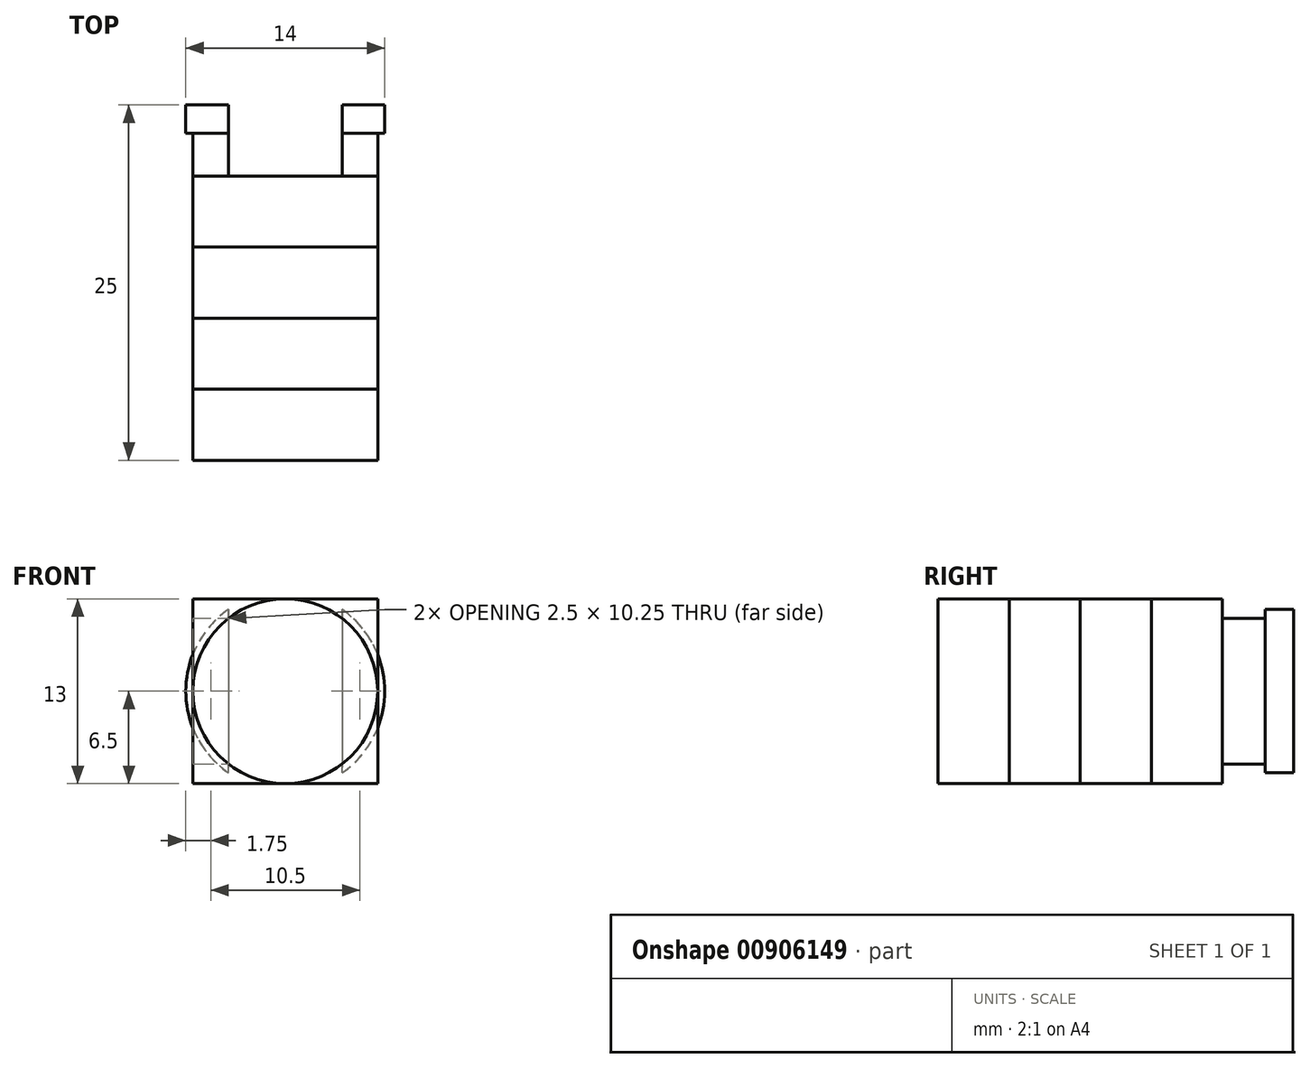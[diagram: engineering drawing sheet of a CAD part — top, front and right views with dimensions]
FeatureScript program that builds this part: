
annotation { "Feature Type Name" : "Feature", "Feature Type Description" : "" }
export const myFeature = defineFeature(function(context is Context, id is Id, definition is map)
    precondition{}
    {
        {
            var Q0;
            Q0=qCreatedBy(makeId("Front.planeOp"),FACE);
            var sketch = newSketch(context, id + "F0", { "sketchPlane" : qUnion([Q0])});
            skCircle(sketch, "E0", {"center": v(0, 0) * mm, "radius": 6.5 * mm});
            skLineSegment(sketch, "E1.rect.bottom", {"start": v(-4, 9.84) * mm, "end": v(4, 9.84) * mm});
            skLineSegment(sketch, "E1.rect.top", {"start": v(-4, -9.84) * mm, "end": v(4, -9.84) * mm});
            skLineSegment(sketch, "E1.rect.left", {"start": v(-4, 9.84) * mm, "end": v(-4, -9.84) * mm});
            skLineSegment(sketch, "E1.rect.right", {"start": v(4, 9.84) * mm, "end": v(4, -9.84) * mm});
            skLineSegment(sketch, "E2", {"start": v(11.65, 0) * mm, "end": v(-11.24, 0) * mm, "construction": true});
            skLineSegment(sketch, "E3", {"start": v(0, -11.93) * mm, "end": v(0, 15.17) * mm, "construction": true});
            skLineSegment(sketch, "E4.rect.bottom", {"start": v(-6.5, -6.5) * mm, "end": v(6.5, -6.5) * mm});
            skLineSegment(sketch, "E4.rect.top", {"start": v(-6.5, 6.5) * mm, "end": v(6.5, 6.5) * mm});
            skLineSegment(sketch, "E4.rect.left", {"start": v(-6.5, -6.5) * mm, "end": v(-6.5, 6.5) * mm});
            skLineSegment(sketch, "E4.rect.right", {"start": v(6.5, -6.5) * mm, "end": v(6.5, 6.5) * mm});
            skSolve(sketch);
        }
        {
            var Q0;
            {var subQ0=sQuery(id+"F0.wireOp",EDGE,"E1.rect.right");var subQ1=sQuery(id+"F0.wireOp",EDGE,"E0");var subQ2=makeQuery(id+"F0.imprint","INTERSECT",VERTEX,{"disambiguationData":[OD(0.0)],"derivedFrom":[subQ1,subQ0]});Q0=makeQuery(id+"F0.imprint","IMPRINT",FACE,{"disambiguationData":[TD([[makeQuery(id+"F0.imprint","IMPRINT",EDGE,{"disambiguationData":[TD([[subQ2,1.0]])],"derivedFrom":subQ1}),1.0]])]});}
            var Q1;
            {var subQ0=sQuery(id+"F0.wireOp",EDGE,"E1.rect.left");var subQ1=sQuery(id+"F0.wireOp",EDGE,"E0");var subQ2=makeQuery(id+"F0.imprint","INTERSECT",VERTEX,{"disambiguationData":[OD(0.0)],"derivedFrom":[subQ1,subQ0]});Q1=makeQuery(id+"F0.imprint","IMPRINT",FACE,{"disambiguationData":[TD([[makeQuery(id+"F0.imprint","IMPRINT",EDGE,{"disambiguationData":[TD([[subQ2,-1.0]])],"derivedFrom":subQ1}),1.0]])]});}
            extrude(context, id + "F1", {"entities" : qUnion([Q0, Q1]), "depth" : 5 * mm});
        }
        {
            var Q0;
            {var subQ0=sQuery(id+"F0.wireOp",EDGE,"E0");var subQ2=sQuery(id+"F0.wireOp",EDGE,"E1.rect.right");var subQ4=makeQuery(id+"F0.imprint","INTERSECT",VERTEX,{"disambiguationData":[OD(0.0)],"derivedFrom":[subQ0,subQ2]});Q0=makeQuery(id+"F0.imprint","IMPRINT",FACE,{"disambiguationData":[TD([[makeQuery(id+"F0.imprint","IMPRINT",EDGE,{"disambiguationData":[TD([[subQ4,-1.0]])],"derivedFrom":subQ0}),1.0]])]});}
            var Q1;
            {var subQ0=sQuery(id+"F0.wireOp",EDGE,"E1.rect.right");var subQ1=sQuery(id+"F0.wireOp",EDGE,"E0");var subQ2=makeQuery(id+"F0.imprint","INTERSECT",VERTEX,{"disambiguationData":[OD(0.0)],"derivedFrom":[subQ1,subQ0]});Q1=makeQuery(id+"F0.imprint","IMPRINT",FACE,{"disambiguationData":[TD([[makeQuery(id+"F0.imprint","IMPRINT",EDGE,{"disambiguationData":[TD([[subQ2,-1.0]])],"derivedFrom":subQ1}),-1.0]])]});}
            var Q2;
            {var subQ1=sQuery(id+"F0.wireOp",EDGE,"E1.rect.bottom");Q2=makeQuery(id+"F0.imprint","IMPRINT",FACE,{"disambiguationData":[TD([[makeQuery(id+"F0.imprint","IMPRINT",EDGE,{"derivedFrom":subQ1}),-1.0]])]});}
            var Q3;
            {var subQ0=sQuery(id+"F0.wireOp",EDGE,"E4.rect.top");var subQ1=sQuery(id+"F0.wireOp",EDGE,"E0");var subQ2=makeQuery(id+"F0.imprint","INTERSECT",VERTEX,{"derivedFrom":[subQ1,subQ0]});Q3=makeQuery(id+"F0.imprint","IMPRINT",FACE,{"disambiguationData":[TD([[makeQuery(id+"F0.imprint","IMPRINT",EDGE,{"disambiguationData":[TD([[subQ2,-1.0]])],"derivedFrom":subQ1}),-1.0]])]});}
            var Q4;
            {var subQ0=sQuery(id+"F0.wireOp",EDGE,"E1.rect.left");var subQ1=sQuery(id+"F0.wireOp",EDGE,"E0");var subQ2=makeQuery(id+"F0.imprint","INTERSECT",VERTEX,{"disambiguationData":[OD(1.0)],"derivedFrom":[subQ1,subQ0]});Q4=makeQuery(id+"F0.imprint","IMPRINT",FACE,{"disambiguationData":[TD([[makeQuery(id+"F0.imprint","IMPRINT",EDGE,{"disambiguationData":[TD([[subQ2,-1.0]])],"derivedFrom":subQ1}),-1.0]])]});}
            var Q5;
            {var subQ0=sQuery(id+"F0.wireOp",EDGE,"E4.rect.bottom");var subQ1=sQuery(id+"F0.wireOp",EDGE,"E0");var subQ2=makeQuery(id+"F0.imprint","INTERSECT",VERTEX,{"derivedFrom":[subQ1,subQ0]});Q5=makeQuery(id+"F0.imprint","IMPRINT",FACE,{"disambiguationData":[TD([[makeQuery(id+"F0.imprint","IMPRINT",EDGE,{"disambiguationData":[TD([[subQ2,-1.0]])],"derivedFrom":subQ1}),-1.0]])]});}
            var Q6;
            {var subQ5=sQuery(id+"F0.wireOp",EDGE,"E1.rect.top");Q6=makeQuery(id+"F0.imprint","IMPRINT",FACE,{"disambiguationData":[TD([[makeQuery(id+"F0.imprint","IMPRINT",EDGE,{"derivedFrom":subQ5}),1.0]])]});}
            var Q7;
            Q7=qSketchRegion(id+"F4",true);
            extrude(context, id + "F2", {"entities" : qUnion([Q0, Q1, Q2, Q3, Q4, Q5, Q6, Q7]), "operationType" : NewBodyOperationType.REMOVE, "depth" : 30 * mm});
        }
        {
            var Q0;
            Q0=makeQuery(id+"F1.opExtrude","CAP_FACE",FACE,{"disambiguationData":[OSD([sQuery(id+"F0.wireOp",EDGE,"E0"),sQuery(id+"F0.wireOp",EDGE,"E1.rect.left")])],"isStart":false});
            cPlane(context, id + "F3", {"entities" : qUnion([Q0]), "cplaneType" : CPlaneType.OFFSET, "offset" : 0 * mm, "width" : 150 * mm, "height" : 150 * mm});
        }
        {
            var Q0;
            Q0=qCreatedBy(id+"F3.planeOp",FACE);
            var sketch = newSketch(context, id + "F4", { "sketchPlane" : qUnion([Q0])});
            skLineSegment(sketch, "E5.rect.bottom", {"start": v(-6.5, -6.5) * mm, "end": v(6.5, -6.5) * mm});
            skLineSegment(sketch, "E5.rect.top", {"start": v(-6.5, 6.5) * mm, "end": v(6.5, 6.5) * mm});
            skLineSegment(sketch, "E5.rect.left", {"start": v(-6.5, -6.5) * mm, "end": v(-6.5, 6.5) * mm});
            skLineSegment(sketch, "E5.rect.right", {"start": v(6.5, -6.5) * mm, "end": v(6.5, 6.5) * mm});
            skPoint(sketch, "E5.rect.middle", {"position": v(0, 0) * mm});
            skCircle(sketch, "E6", {"center": v(0, 0) * mm, "radius": 6.5 * mm});
            skLineSegment(sketch, "E7", {"start": v(-8.74, 0) * mm, "end": v(9.18, 0) * mm, "construction": true});
            skLineSegment(sketch, "E8", {"start": v(0, 9.31) * mm, "end": v(0, -14.04) * mm, "construction": true});
            skSolve(sketch);
        }
        {
            var Q0;
            {var subQ0=sQuery(id+"F4.wireOp",EDGE,"E5.rect.bottom");Q0=makeQuery(id+"F4.imprint","IMPRINT",FACE,{"disambiguationData":[TD([[makeQuery(id+"F4.imprint","IMPRINT",EDGE,{"derivedFrom":subQ0}),1.0]])]});}
            var Q1;
            {var subQ0=sQuery(id+"F4.wireOp",EDGE,"E5.rect.top");Q1=makeQuery(id+"F4.imprint","IMPRINT",FACE,{"disambiguationData":[TD([[makeQuery(id+"F4.imprint","IMPRINT",EDGE,{"derivedFrom":subQ0}),-1.0]])]});}
            extrude(context, id + "F5", {"entities" : qUnion([Q0, Q1]), "operationType" : NewBodyOperationType.ADD, "depth" : 5 * mm});
        }
        {
            var Q0;
            {var subQ0=sQuery(id+"F4.wireOp",EDGE,"E6");var subQ1=makeQuery(id+"F4.imprint","INTERSECT",VERTEX,{"derivedFrom":[sQuery(id+"F4.wireOp",EDGE,"E5.rect.top"),subQ0]});Q0=makeQuery(id+"F4.imprint","IMPRINT",FACE,{"disambiguationData":[TD([[makeQuery(id+"F4.imprint","IMPRINT",EDGE,{"disambiguationData":[TD([[subQ1,1.0]])],"derivedFrom":subQ0}),1.0]])]});}
            extrude(context, id + "F6", {"entities" : qUnion([Q0]), "operationType" : NewBodyOperationType.ADD, "depth" : 10 * mm});
        }
        {
            var Q0;
            Q0=makeQuery(id+"F6.opExtrude","CAP_FACE",FACE,{"disambiguationData":[OSD([sQuery(id+"F4.wireOp",EDGE,"E5.rect.left"),sQuery(id+"F4.wireOp",EDGE,"E5.rect.right"),sQuery(id+"F4.wireOp",EDGE,"E6")])],"isStart":false});
            cPlane(context, id + "F7", {"entities" : qUnion([Q0]), "cplaneType" : CPlaneType.OFFSET, "offset" : 0 * mm, "width" : 150 * mm, "height" : 150 * mm});
        }
        {
            var Q0;
            Q0=qCreatedBy(id+"F7.planeOp",FACE);
            var sketch = newSketch(context, id + "F8", { "sketchPlane" : qUnion([Q0])});
            skCircle(sketch, "E9", {"center": v(0, 0) * mm, "radius": 6.5 * mm});
            skLineSegment(sketch, "E10.rect.bottom", {"start": v(-6.5, 6.5) * mm, "end": v(6.5, 6.5) * mm});
            skLineSegment(sketch, "E10.rect.top", {"start": v(-6.5, -6.5) * mm, "end": v(6.5, -6.5) * mm});
            skLineSegment(sketch, "E10.rect.left", {"start": v(-6.5, 6.5) * mm, "end": v(-6.5, -6.5) * mm});
            skLineSegment(sketch, "E10.rect.right", {"start": v(6.5, 6.5) * mm, "end": v(6.5, -6.5) * mm});
            skSolve(sketch);
        }
        {
            var Q0;
            {var subQ0=sQuery(id+"F8.wireOp",EDGE,"E10.rect.bottom");var subQ1=sQuery(id+"F8.wireOp",EDGE,"E9");var subQ2=makeQuery(id+"F8.imprint","INTERSECT",VERTEX,{"derivedFrom":[subQ1,subQ0]});Q0=makeQuery(id+"F8.imprint","IMPRINT",FACE,{"disambiguationData":[TD([[makeQuery(id+"F8.imprint","IMPRINT",EDGE,{"disambiguationData":[TD([[subQ2,-1.0]])],"derivedFrom":subQ1}),-1.0]])]});}
            var Q1;
            {var subQ0=sQuery(id+"F8.wireOp",EDGE,"E10.rect.bottom");var subQ1=sQuery(id+"F8.wireOp",EDGE,"E9");var subQ2=makeQuery(id+"F8.imprint","INTERSECT",VERTEX,{"derivedFrom":[subQ1,subQ0]});Q1=makeQuery(id+"F8.imprint","IMPRINT",FACE,{"disambiguationData":[TD([[makeQuery(id+"F8.imprint","IMPRINT",EDGE,{"disambiguationData":[TD([[subQ2,1.0]])],"derivedFrom":subQ1}),-1.0]])]});}
            var Q2;
            {var subQ0=sQuery(id+"F8.wireOp",EDGE,"E10.rect.right");var subQ1=sQuery(id+"F8.wireOp",EDGE,"E9");var subQ2=makeQuery(id+"F8.imprint","INTERSECT",VERTEX,{"derivedFrom":[subQ1,subQ0]});Q2=makeQuery(id+"F8.imprint","IMPRINT",FACE,{"disambiguationData":[TD([[makeQuery(id+"F8.imprint","IMPRINT",EDGE,{"disambiguationData":[TD([[subQ2,1.0]])],"derivedFrom":subQ1}),-1.0]])]});}
            var Q3;
            {var subQ0=sQuery(id+"F8.wireOp",EDGE,"E10.rect.left");var subQ1=sQuery(id+"F8.wireOp",EDGE,"E9");var subQ2=makeQuery(id+"F8.imprint","INTERSECT",VERTEX,{"derivedFrom":[subQ1,subQ0]});Q3=makeQuery(id+"F8.imprint","IMPRINT",FACE,{"disambiguationData":[TD([[makeQuery(id+"F8.imprint","IMPRINT",EDGE,{"disambiguationData":[TD([[subQ2,-1.0]])],"derivedFrom":subQ1}),-1.0]])]});}
            extrude(context, id + "F9", {"entities" : qUnion([Q0, Q1, Q2, Q3]), "operationType" : NewBodyOperationType.ADD, "depth" : 5 * mm});
        }
        {
            var Q0;
            {var subQ0=sQuery(id+"F8.wireOp",EDGE,"E9");var subQ1=makeQuery(id+"F8.imprint","INTERSECT",VERTEX,{"derivedFrom":[subQ0,sQuery(id+"F8.wireOp",EDGE,"E10.rect.bottom")]});Q0=makeQuery(id+"F8.imprint","IMPRINT",FACE,{"disambiguationData":[TD([[makeQuery(id+"F8.imprint","IMPRINT",EDGE,{"disambiguationData":[TD([[subQ1,1.0]])],"derivedFrom":subQ0}),1.0]])]});}
            extrude(context, id + "F10", {"entities" : qUnion([Q0]), "operationType" : NewBodyOperationType.ADD, "depth" : 10 * mm});
        }
        {
            var Q0;
            {var subQ0=sQuery(id+"F0.wireOp",EDGE,"E0");var subQ1=makeQuery(id+"F0.imprint","INTERSECT",VERTEX,{"derivedFrom":[subQ0,sQuery(id+"F0.wireOp",EDGE,"E4.rect.right")]});Q0=makeQuery(id+"F0.imprint","IMPRINT",FACE,{"disambiguationData":[TD([[makeQuery(id+"F0.imprint","IMPRINT",EDGE,{"disambiguationData":[TD([[subQ1,-1.0]])],"derivedFrom":subQ0}),1.0]])]});}
            cPlane(context, id + "F11", {"entities" : qUnion([Q0]), "cplaneType" : CPlaneType.OFFSET, "offset" : 0 * mm, "width" : 150 * mm, "height" : 150 * mm});
        }
        {
            var Q0;
            Q0=qCreatedBy(id+"F11.planeOp",FACE);
            var sketch = newSketch(context, id + "F12", { "sketchPlane" : qUnion([Q0])});
            skCircle(sketch, "E11", {"center": v(0, 0) * mm, "radius": 7 * mm});
            skCircle(sketch, "E12", {"center": v(0, 0) * mm, "radius": 6.5 * mm});
            skLineSegment(sketch, "E13.rect.bottom", {"start": v(-4, 11.58) * mm, "end": v(4, 11.58) * mm});
            skLineSegment(sketch, "E13.rect.top", {"start": v(-4, -11.58) * mm, "end": v(4, -11.58) * mm});
            skLineSegment(sketch, "E13.rect.left", {"start": v(-4, 11.58) * mm, "end": v(-4, -11.58) * mm});
            skLineSegment(sketch, "E13.rect.right", {"start": v(4, 11.58) * mm, "end": v(4, -11.58) * mm});
            skSolve(sketch);
        }
        {
            var Q0;
            Q0=makeQuery(id+"F12.imprint","IMPRINT",FACE,{"disambiguationData":[TD([[makeQuery(id+"F12.imprint","IMPRINT",EDGE,{"derivedFrom":sQuery(id+"F12.wireOp",EDGE,"E11")}),1.0]])]});
            extrude(context, id + "F13", {"entities" : qUnion([Q0]), "operationType" : NewBodyOperationType.ADD, "depth" : 2 * mm});
        }
        {
            var Q0;
            {var subQ5=sQuery(id+"F12.wireOp",EDGE,"E13.rect.bottom");Q0=makeQuery(id+"F12.imprint","IMPRINT",FACE,{"disambiguationData":[TD([[makeQuery(id+"F12.imprint","IMPRINT",EDGE,{"derivedFrom":subQ5}),-1.0]])]});}
            var Q1;
            {var subQ5=sQuery(id+"F12.wireOp",EDGE,"E13.rect.top");Q1=makeQuery(id+"F12.imprint","IMPRINT",FACE,{"disambiguationData":[TD([[makeQuery(id+"F12.imprint","IMPRINT",EDGE,{"derivedFrom":subQ5}),1.0]])]});}
            var Q2;
            {var subQ0=sQuery(id+"F12.wireOp",EDGE,"E13.rect.left");var subQ1=sQuery(id+"F12.wireOp",EDGE,"E11");var subQ2=makeQuery(id+"F12.imprint","INTERSECT",VERTEX,{"disambiguationData":[OD(0.0)],"derivedFrom":[subQ1,subQ0]});Q2=makeQuery(id+"F12.imprint","IMPRINT",FACE,{"disambiguationData":[TD([[makeQuery(id+"F12.imprint","IMPRINT",EDGE,{"disambiguationData":[TD([[subQ2,1.0]])],"derivedFrom":subQ1}),1.0]])]});}
            var Q3;
            {var subQ0=sQuery(id+"F12.wireOp",EDGE,"E13.rect.left");var subQ1=sQuery(id+"F12.wireOp",EDGE,"E11");var subQ2=makeQuery(id+"F12.imprint","INTERSECT",VERTEX,{"disambiguationData":[OD(1.0)],"derivedFrom":[subQ1,subQ0]});Q3=makeQuery(id+"F12.imprint","IMPRINT",FACE,{"disambiguationData":[TD([[makeQuery(id+"F12.imprint","IMPRINT",EDGE,{"disambiguationData":[TD([[subQ2,-1.0]])],"derivedFrom":subQ1}),1.0]])]});}
            extrude(context, id + "F14", {"entities" : qUnion([Q0, Q1, Q2, Q3]), "operationType" : NewBodyOperationType.REMOVE, "depth" : 3 * mm});
        }
        {
            var Q0;
            Q0=makeQuery(id+"F1.opExtrude","SWEPT_BODY",BODY,{"disambiguationData":[OSD([sQuery(id+"F0.wireOp",EDGE,"E0"),sQuery(id+"F0.wireOp",EDGE,"E1.rect.right")])]});
            transform(context, id + "F15", {"entities" : qUnion([Q0]), "transformType" : TransformType.TRANSLATION_3D, "dx" : 0 * mm, "dy" : 0 * mm, "dz" : 0 * mm, "makeCopy" : true});
        }
    });
